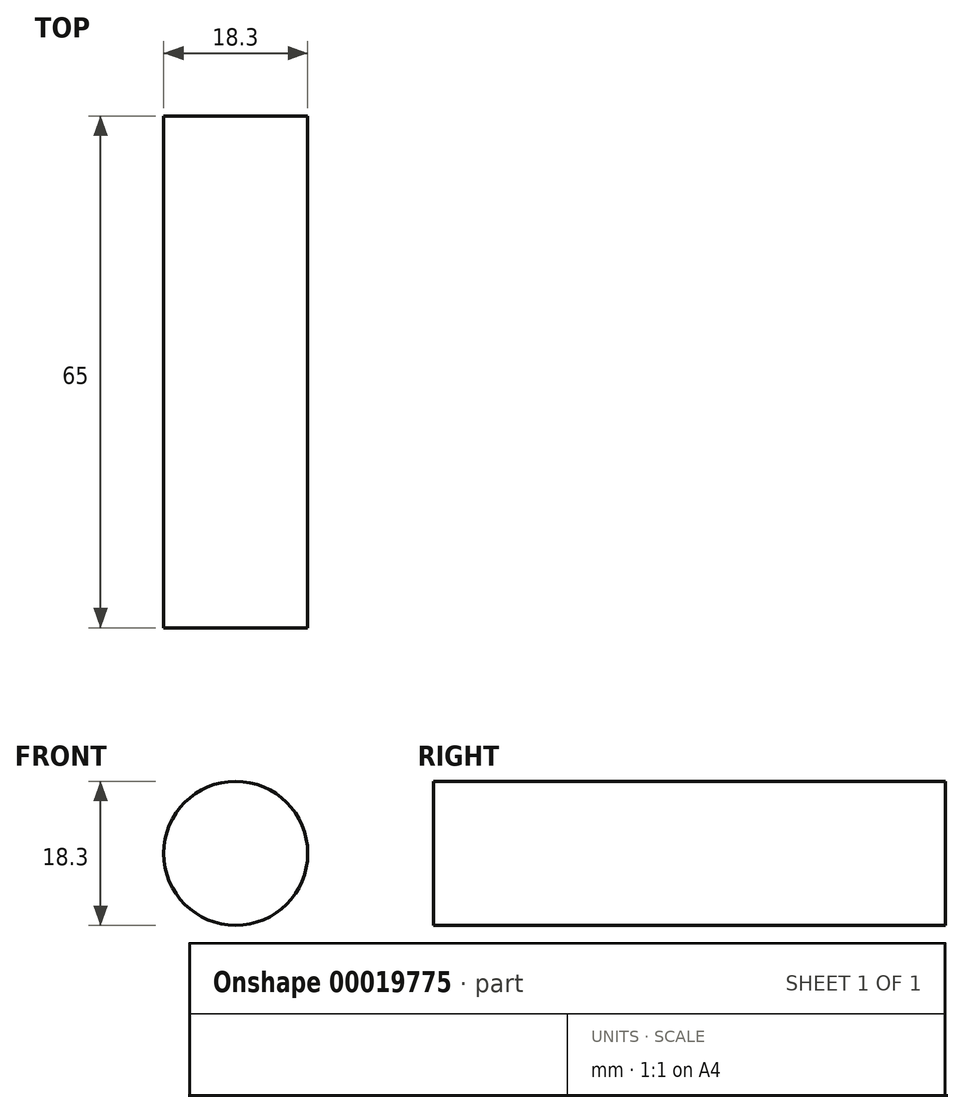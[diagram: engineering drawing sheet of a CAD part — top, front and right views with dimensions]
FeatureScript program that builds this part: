
annotation { "Feature Type Name" : "Feature", "Feature Type Description" : "" }
export const myFeature = defineFeature(function(context is Context, id is Id, definition is map)
    precondition{}
    {
        {
            var Q0;
            Q0=qCreatedBy(makeId("Front.planeOp"),FACE);
            var sketch = newSketch(context, id + "F0", { "sketchPlane" : qUnion([Q0])});
            skCircle(sketch, "E0", {"center": v(0, 0) * mm, "radius": 9.15 * mm});
            skSolve(sketch);
        }
        {
            var Q0;
            Q0 = qSketchRegion(id + "F0", true);
            extrude(context, id + "F1", {"entities" : qUnion([Q0]), "oppositeDirection" : true, "depth" : 65 * mm});
        }
    });
